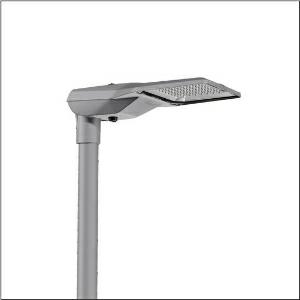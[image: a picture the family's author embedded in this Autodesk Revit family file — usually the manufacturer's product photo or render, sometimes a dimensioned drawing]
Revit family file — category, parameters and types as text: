
# Revit family: streetlight_sl_21_iq_midi___p0_5a_5xe3v31y08nb_ca8d
name_source: partatom
category: Lighting Fixtures
units: mm (PartAtom-declared; Revit-internal decimal feet)

## family parameters
Cut with Voids When Loaded = No
Host = Face
Light Source = No
Part Type = Normal
Room Calculation Point = No
Round Connector Dimension = Use Diameter
Shared = No

## types (1)
- --- (1 x LED, 21180 lm, 136.6 W, 3000K)
    Apparent Load = 137 VA
    CIE Flux Codes = 37 73 96 100 100
    Color Rendering = 70
    Color Temperature = 3000K
    Default Elevation = 1800 mm
    Description = Streetlight SL 21 iQ midi, mast luminaire, primary light control with lens, of PMMA, primary optical cover: cover, of toughened safety glass, transparent, light distribution: P0.5a, light emission: direct distribution, primary light characteristic: asymmetric, installation type: post-top, side-entry, LED, High Power LED, rated luminous flux: 21.180lm, luminous efficacy: 155lm/W, light colour: 730, colour temperature: 3000K, control gear: iQ-Street Remote, D4i with power reduction, control: pre-setting: logarithmic dimming characteristic, Street-Remote, Auto-Match, Temp-Guard, Lumen-Switch, Night-Set, Smart-Wire, Light-Fading, Desk-Remote (wireless, voltage-free reading and setting of iQ features in the workshop via application-optimized NFC function/RFID function), optimised constant luminous flux control (CLO 2.0), mains connection: 230..240V, AC, 50/60Hz, start of lifetime: 137W, end of service life: 144W, reduction: 61W, luminaire housing, of diecast aluminium, powder-coated, Siteco® metallic grey (DB 702S), corrosivity category C5 mid according to DIN EN ISO 12944, please order mast flange separately, inclination adjustable: 0°, 5°, 10°, 15°, sealing non-destructively replaceable, multi-level sealing system, length: 644mm, width: 335mm, height: 110mm, mast flange for spigot size: 42mm (side-entry): 5XC10008XM4, 60/48mm (side-entry/post-top): 5XC10108XM2, 76/60mm (side-entry/post-top): 5XC10108XM1, mounting height: 4..8m, Smart Interface below and above, protection rating (complete): IP66, insulation class (complete): insulation class II (safety insulation), certification: CE, ENEC, ENEC+, VDE, impact resistance: IK10, permissible operating ambient temperature for outdoor applications: -40..+50°C, standard-compliant lighting for roads and squares, packaging unit: 1 piece

Light Distribution: P0.5a
    Height = 111 mm
    Lamp = 1 x LED
    Lamp Light Flux = 21180 lm
    Lamp Power = 136.6 W
    Lamp count = 1
    Length = 644 mm
    Luminous efficacy = 155 lm/W
    Manufacturer = Siteco
    ModVariant = No
    Model = 5XE3V31Y08NB
    Number of Poles = 1
    OnlyDefault = Yes
    Power Factor = 1
    Product Name = Streetlight SL 21 iQ midi | P0.5a
    Product group = mast luminaire | pylon top
    ProductGroupID = 6100
    Protection Class = Protection class II
    Protection Degree = IP 66
    RLX_Detail_Level = 1
    RLX_Emergency_Light_Flux = 0 lm
    RLX_Emergency_Type = 0
    RLX_Emergency_Type_DB = No
    RlxData = <blob elided: 27053 chars, md5=3731fa01>
    Socket = socket
    Standby Power = 0 W
    System Light Flux = 21180 lm
    System Power = 137 W
    Type Comments = factory setting: luminous flux: 100 % | dim-lin: 254 | 733 mA
    Type Image = l_1004304.jpg
    URL = http://relux.com
    VarID = @adj_069274
    Voltage = 0 V
    Weight = 0.00 kg
    Width = 336 mm

## geometry (parser evidence)
native form markers: Blend x4, Sweep x9
no freeform markers — native parametric forms only
